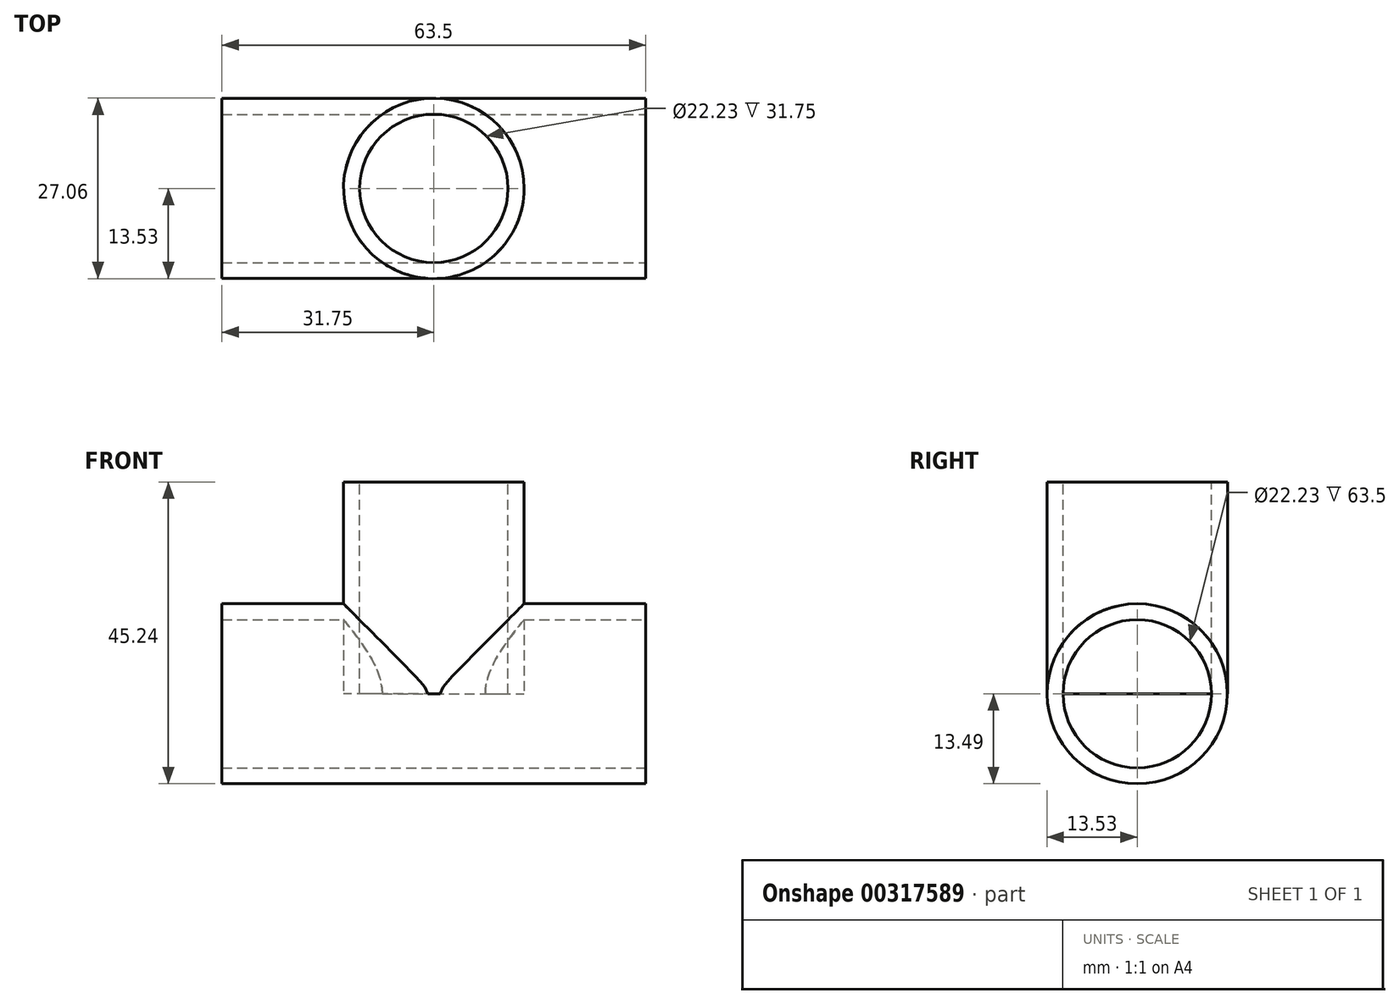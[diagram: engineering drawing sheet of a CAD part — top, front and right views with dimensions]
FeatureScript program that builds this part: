
annotation { "Feature Type Name" : "Feature", "Feature Type Description" : "" }
export const myFeature = defineFeature(function(context is Context, id is Id, definition is map)
    precondition{}
    {
        {
            var Q0;
            Q0=qCreatedBy(makeId("Right.planeOp"),FACE);
            var sketch = newSketch(context, id + "F0", { "sketchPlane" : qUnion([Q0])});
            skCircle(sketch, "E0", {"center": v(0, 0) * mm, "radius": 13.5 * mm});
            skSolve(sketch);
        }
        {
            var Q0;
            Q0=makeQuery(id+"F0.imprint","IMPRINT",FACE,{"disambiguationData":[TD([[makeQuery(id+"F0.imprint","IMPRINT",EDGE,{"derivedFrom":sQuery(id+"F0.wireOp",EDGE,"E0")}),1.0]])]});
            extrude(context, id + "F1", {"entities" : qUnion([Q0]), "endBound" : BoundingType.SYMMETRIC, "depth" : 63.5 * mm});
        }
        {
            var Q0;
            Q0=makeQuery(id+"F1.opExtrude","CAP_FACE",FACE,{"disambiguationData":[OSD([sQuery(id+"F0.wireOp",EDGE,"E0")])],"isStart":false});
            var sketch = newSketch(context, id + "F2", { "sketchPlane" : qUnion([Q0])});
            skCircle(sketch, "E1", {"center": v(0, 0) * mm, "radius": 11.11 * mm});
            skSolve(sketch);
        }
        {
            var Q0;
            Q0=sQuery(id+"F2.wireOp",VERTEX,"E1.center");
            var Q1;
            Q1=makeQuery(id+"F1.opExtrude","SWEPT_BODY",BODY,{"disambiguationData":[OSD([sQuery(id+"F0.wireOp",EDGE,"E0")])]});
            hole(context, id + "F3", {"style" : HoleStyle.SIMPLE, "endStyle" : HoleEndStyle.THROUGH, "holeDiameter" : 22.22 * mm, "tappedDepth" : 12.7 * mm, "tapClearance" : 3, "locations" : qUnion([Q0]), "scope" : qUnion([Q1])});
        }
        {
            var Q0;
            Q0=qCreatedBy(makeId("Top.planeOp"),FACE);
            var sketch = newSketch(context, id + "F4", { "sketchPlane" : qUnion([Q0])});
            skCircle(sketch, "E2", {"center": v(0, 0) * mm, "radius": 13.53 * mm});
            skSolve(sketch);
        }
        {
            var Q0;
            Q0=makeQuery(id+"F4.imprint","IMPRINT",FACE,{"disambiguationData":[TD([[makeQuery(id+"F4.imprint","IMPRINT",EDGE,{"derivedFrom":sQuery(id+"F4.wireOp",EDGE,"E2")}),1.0]])]});
            extrude(context, id + "F5", {"entities" : qUnion([Q0]), "operationType" : NewBodyOperationType.ADD, "depth" : 31.75 * mm});
        }
        {
            var Q0;
            Q0=makeQuery(id+"F5.opExtrude","CAP_FACE",FACE,{"disambiguationData":[OSD([sQuery(id+"F4.wireOp",EDGE,"E2")])],"isStart":false});
            var sketch = newSketch(context, id + "F6", { "sketchPlane" : qUnion([Q0])});
            skCircle(sketch, "E3", {"center": v(0, 0) * mm, "radius": 11.11 * mm});
            skSolve(sketch);
        }
        {
            var Q0;
            Q0=sQuery(id+"F6.wireOp",VERTEX,"E3.center");
            var Q1;
            Q1=makeQuery(id+"F1.opExtrude","SWEPT_BODY",BODY,{"disambiguationData":[OSD([sQuery(id+"F0.wireOp",EDGE,"E0")])]});
            hole(context, id + "F7", {"style" : HoleStyle.SIMPLE, "endStyle" : HoleEndStyle.BLIND, "holeDiameter" : 22.22 * mm, "holeDepth" : 31.75 * mm, "tappedDepth" : 12.7 * mm, "tapClearance" : 3, "locations" : qUnion([Q0]), "scope" : qUnion([Q1])});
        }
    });
